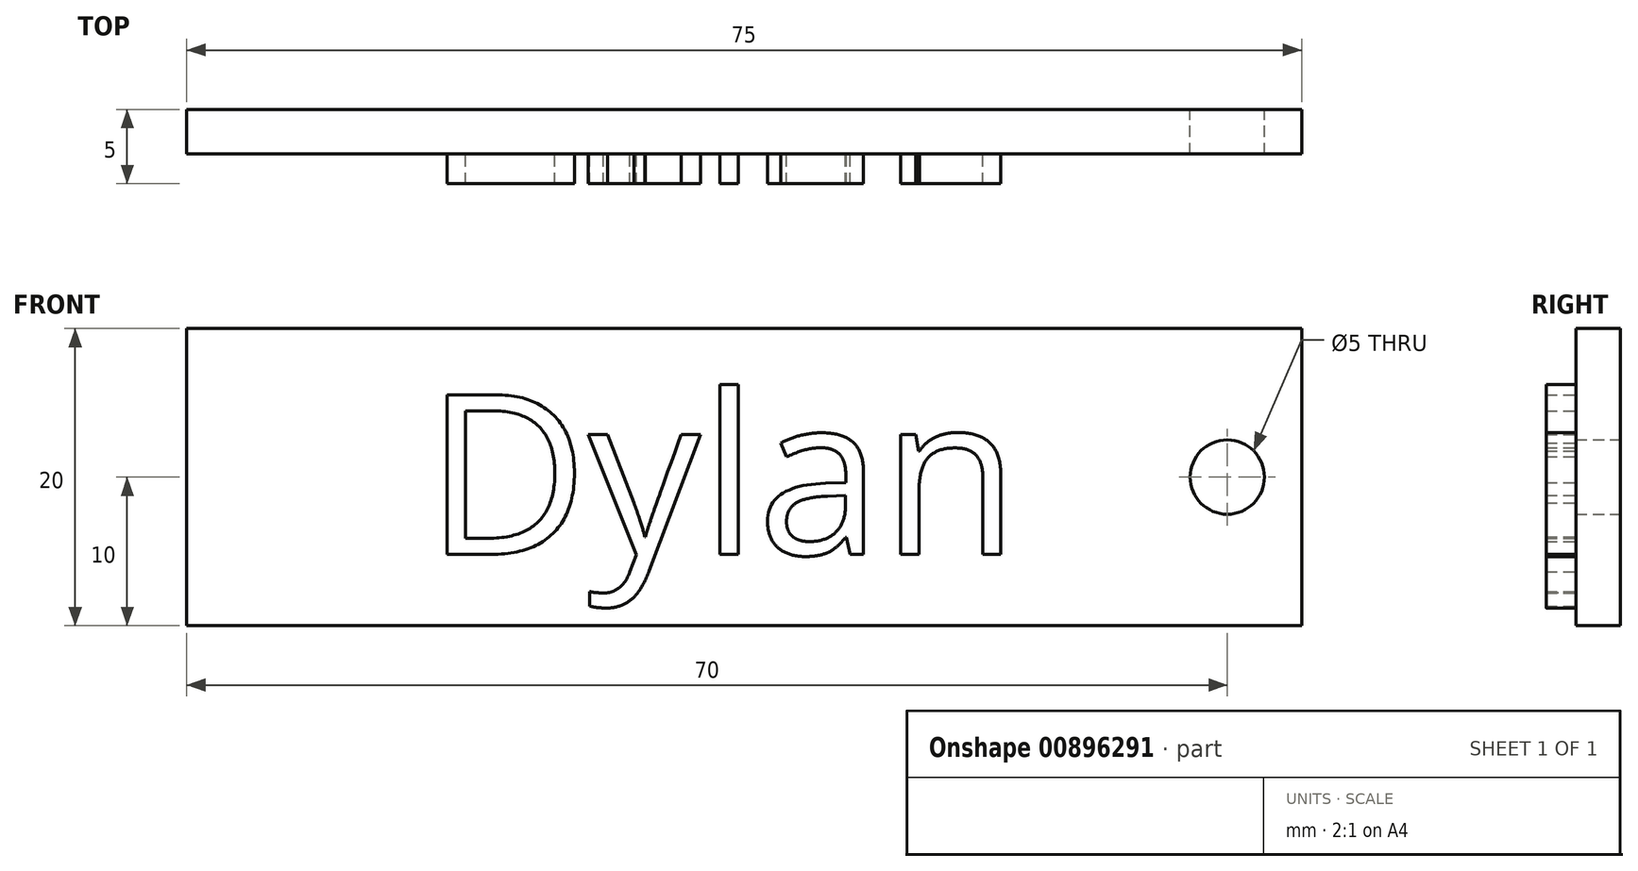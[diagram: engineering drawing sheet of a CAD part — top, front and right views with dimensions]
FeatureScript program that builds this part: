
annotation { "Feature Type Name" : "Feature", "Feature Type Description" : "" }
export const myFeature = defineFeature(function(context is Context, id is Id, definition is map)
    precondition{}
    {
        {
            var Q0;
            Q0=qCreatedBy(makeId("Front.planeOp"),FACE);
            var sketch = newSketch(context, id + "F0", { "sketchPlane" : qUnion([Q0])});
            skLineSegment(sketch, "E0.bottom", {"start": v(0, 0) * mm, "end": v(75, 0) * mm});
            skLineSegment(sketch, "E0.top", {"start": v(0, -20) * mm, "end": v(75, -20) * mm});
            skLineSegment(sketch, "E0.left", {"start": v(0, 0) * mm, "end": v(0, -20) * mm});
            skLineSegment(sketch, "E0.right", {"start": v(75, 0) * mm, "end": v(75, -20) * mm});
            skCircle(sketch, "E1", {"center": v(-102.43, 116.93) * mm, "radius": 4.75 * mm});
            skCircle(sketch, "E2", {"center": v(-97.91, 115.45) * mm, "radius": 1.42 * mm});
            skCircle(sketch, "E3", {"center": v(70, -10) * mm, "radius": 2.5 * mm});
            skSolve(sketch);
        }
        {
            var Q0;
            Q0=makeQuery(id+"F0.imprint","IMPRINT",FACE,{"disambiguationData":[TD([[makeQuery(id+"F0.imprint","IMPRINT",EDGE,{"derivedFrom":sQuery(id+"F0.wireOp",EDGE,"E0.bottom")}),-1.0]])]});
            extrude(context, id + "F1", {"entities" : qUnion([Q0]), "depth" : 3 * mm, "offsetDistance" : 25 * mm});
        }
        {
            var Q0;
            Q0=makeQuery(id+"F1.opExtrude","CAP_FACE",FACE,{"disambiguationData":[OSD([sQuery(id+"F0.wireOp",EDGE,"E0.bottom"),sQuery(id+"F0.wireOp",EDGE,"E0.top"),sQuery(id+"F0.wireOp",EDGE,"E0.left"),sQuery(id+"F0.wireOp",EDGE,"E0.right"),sQuery(id+"F0.wireOp",EDGE,"E3")])],"isStart":false});
            var sketch = newSketch(context, id + "F2", { "sketchPlane" : qUnion([Q0])});
            skText(sketch, "E4", { "text": "Dylan", "fontName": "OpenSans-Regular.ttf"});
            const initialGuessF2  = {"E4": [0.01603, -0.0152, 1, 0, 0.01083]};
            skSetInitialGuess(sketch, initialGuessF2);
            skSolve(sketch);
        }
        {
            var Q0;
            Q0 = qSketchRegion(id + "F2", true);
            extrude(context, id + "F3", {"entities" : qUnion([Q0]), "operationType" : NewBodyOperationType.ADD, "depth" : 2 * mm, "offsetDistance" : 25 * mm});
        }
    });
